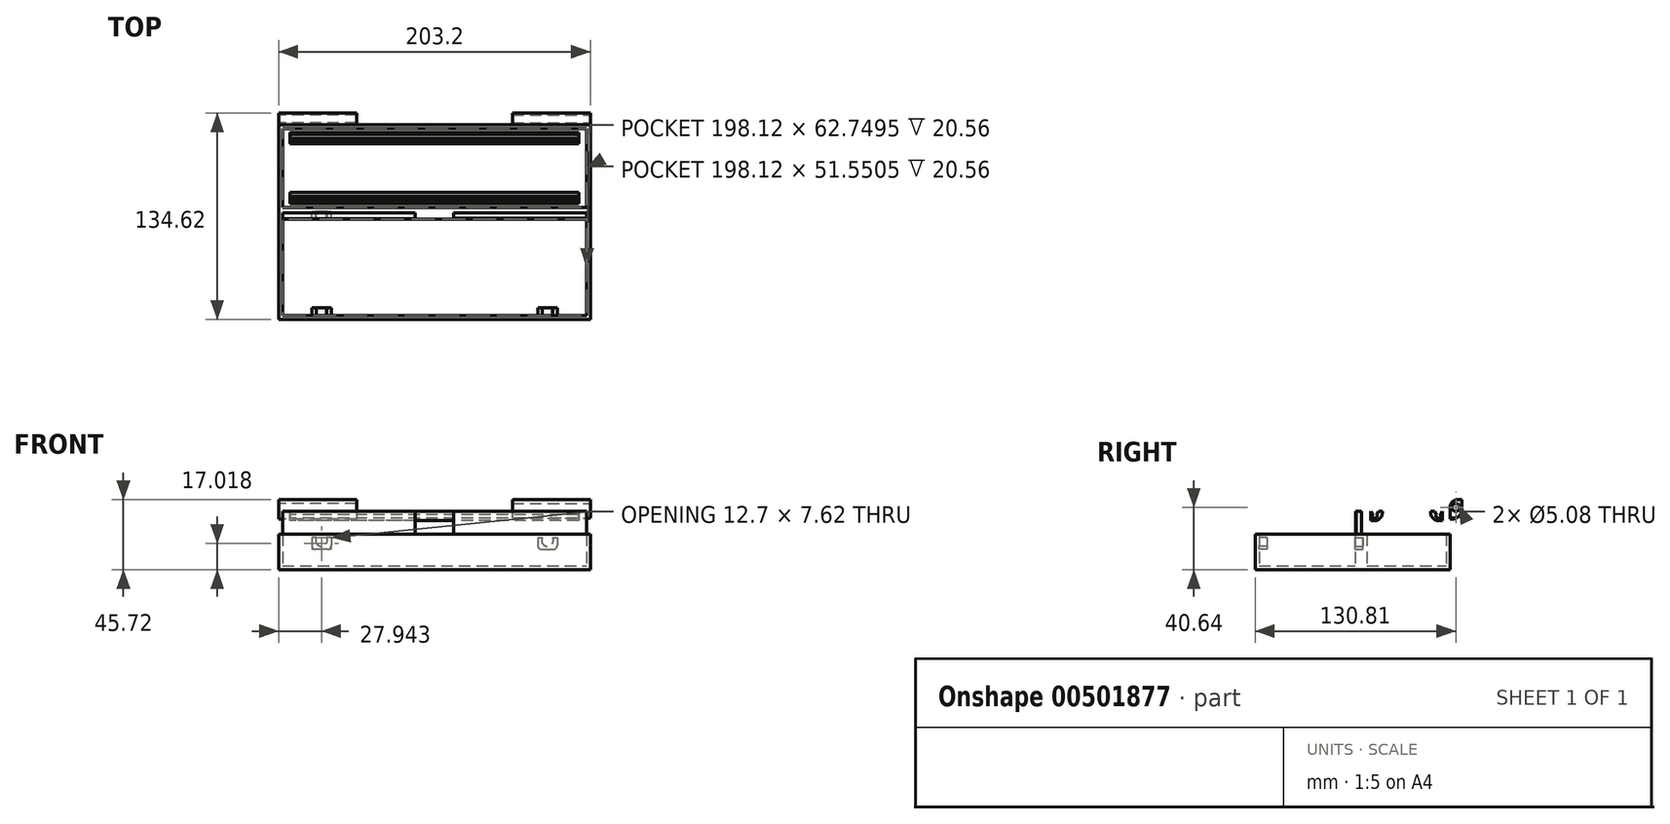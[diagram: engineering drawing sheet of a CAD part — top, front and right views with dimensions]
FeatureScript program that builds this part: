
annotation { "Feature Type Name" : "Feature", "Feature Type Description" : "" }
export const myFeature = defineFeature(function(context is Context, id is Id, definition is map)
    precondition{}
    {
        {
            var Q0;
            Q0=qCreatedBy(makeId("Top.planeOp"),FACE);
            var sketch = newSketch(context, id + "F0", { "sketchPlane" : qUnion([Q0])});
            skLineSegment(sketch, "E0.bottom", {"start": v(-95.04, -72.9) * mm, "end": v(108.16, -72.9) * mm});
            skLineSegment(sketch, "E0.top", {"start": v(-95.04, 54.1) * mm, "end": v(108.16, 54.1) * mm});
            skLineSegment(sketch, "E0.left", {"start": v(-95.04, -72.9) * mm, "end": v(-95.04, 54.1) * mm});
            skLineSegment(sketch, "E0.right", {"start": v(108.16, -72.9) * mm, "end": v(108.16, 54.1) * mm});
            skSolve(sketch);
        }
        {
            var Q0;
            Q0 = qSketchRegion(id + "F0", true);
            extrude(context, id + "F1", {"entities" : qUnion([Q0]), "endBound" : BoundingType.SYMMETRIC, "depth" : 38.1 * mm});
        }
        {
            var Q0;
            Q0=makeQuery(id+"F1.opExtrude","CAP_FACE",FACE,{"disambiguationData":[OSD([sQuery(id+"F0.wireOp",EDGE,"E0.bottom"),sQuery(id+"F0.wireOp",EDGE,"E0.top"),sQuery(id+"F0.wireOp",EDGE,"E0.left"),sQuery(id+"F0.wireOp",EDGE,"E0.right")])],"isStart":false});
            shell(context, id + "F2", {"entities" : qUnion([Q0]), "thickness" : 2.54 * mm});
        }
        {
            var Q0;
            Q0=makeQuery(id+"F2.opShell","OFFSET_FACE",FACE,{"disambiguationData":[OSD([sQuery(id+"F0.wireOp",EDGE,"E0.bottom"),sQuery(id+"F0.wireOp",EDGE,"E0.top"),sQuery(id+"F0.wireOp",EDGE,"E0.left"),sQuery(id+"F0.wireOp",EDGE,"E0.right")])]});
            var sketch = newSketch(context, id + "F3", { "sketchPlane" : qUnion([Q0])});
            skLineSegment(sketch, "E1", {"start": v(-92.5, 0) * mm, "end": v(105.62, 0) * mm});
            skLineSegment(sketch, "E2", {"start": v(-92.5, -2.54) * mm, "end": v(105.62, -2.54) * mm});
            skLineSegment(sketch, "E3", {"start": v(-92.5, 0) * mm, "end": v(-92.5, -2.54) * mm});
            skLineSegment(sketch, "E4", {"start": v(105.62, 0) * mm, "end": v(105.62, -2.54) * mm});
            skSolve(sketch);
        }
        {
            var Q0;
            Q0 = qSketchRegion(id + "F3", true);
            var Q1;
            Q1=makeQuery(id+"F1.opExtrude","CAP_FACE",FACE,{"disambiguationData":[OSD([sQuery(id+"F0.wireOp",EDGE,"E0.bottom"),sQuery(id+"F0.wireOp",EDGE,"E0.top"),sQuery(id+"F0.wireOp",EDGE,"E0.left"),sQuery(id+"F0.wireOp",EDGE,"E0.right")])],"isStart":false});
            extrude(context, id + "F4", {"entities" : qUnion([Q0]), "operationType" : NewBodyOperationType.ADD, "endBound" : BoundingType.UP_TO_SURFACE, "endBoundEntityFace" : qUnion([Q1]), "depth" : 25.4 * mm});
        }
        {
            var Q0;
            Q0=makeQuery(id+"F4.opExtrude","SWEPT_FACE",FACE,{"disambiguationData":[OSD([sQuery(id+"F3.wireOp",EDGE,"E2")])]});
            var sketch = newSketch(context, id + "F5", { "sketchPlane" : qUnion([Q0])});
            skArc(sketch, "E5", {"start": v(76.85, 1.78) * mm, "mid": v(80.22, -3.8) * mm, "end": v(83.6, 1.78) * mm});
            skLineSegment(sketch, "E6", {"start": v(76.85, 1.78) * mm, "end": v(73.87, 1.78) * mm});
            skLineSegment(sketch, "E7", {"start": v(73.87, 1.78) * mm, "end": v(73.87, -3.3) * mm});
            skLineSegment(sketch, "E8", {"start": v(76.41, -5.84) * mm, "end": v(84.03, -5.84) * mm});
            skLineSegment(sketch, "E9", {"start": v(86.57, -3.3) * mm, "end": v(86.57, 1.78) * mm});
            skLineSegment(sketch, "E10", {"start": v(86.57, 1.78) * mm, "end": v(83.6, 1.78) * mm});
            skPoint(sketch, "E11.visualSharp", {"position": v(73.87, -5.84) * mm});
            skArc(sketch, "E11.filletArc", {"start": v(73.87, -3.3) * mm, "mid": v(74.62, -5.1) * mm, "end": v(76.41, -5.84) * mm});
            skPoint(sketch, "E12.visualSharp", {"position": v(86.57, -5.84) * mm});
            skArc(sketch, "E12.filletArc", {"start": v(84.03, -5.84) * mm, "mid": v(85.83, -5.1) * mm, "end": v(86.57, -3.3) * mm});
            skLineSegment(sketch, "E13", {"start": v(6.56, 19.05) * mm, "end": v(6.56, -16.5) * mm, "construction": true});
            skArc(sketch, "E14.MirrorCS", {"start": v(-60.75, -3.3) * mm, "mid": v(-61.5, -5.1) * mm, "end": v(-63.29, -5.84) * mm});
            skPoint(sketch, "E15.MirrorP", {"position": v(-60.75, -5.84) * mm});
            skLineSegment(sketch, "E16.MirrorCS", {"start": v(-63.29, -5.84) * mm, "end": v(-70.9, -5.84) * mm});
            skPoint(sketch, "E17.MirrorP", {"position": v(-73.45, -5.84) * mm});
            skArc(sketch, "E18.MirrorCS", {"start": v(-70.9, -5.84) * mm, "mid": v(-72.7, -5.1) * mm, "end": v(-73.45, -3.3) * mm});
            skLineSegment(sketch, "E19.MirrorCS", {"start": v(-73.45, 1.78) * mm, "end": v(-70.47, 1.78) * mm});
            skLineSegment(sketch, "E20.MirrorCS", {"start": v(-73.45, -3.3) * mm, "end": v(-73.45, 1.78) * mm});
            skArc(sketch, "E21.MirrorCS", {"start": v(-63.73, 1.78) * mm, "mid": v(-67.1, -3.8) * mm, "end": v(-70.47, 1.78) * mm});
            skLineSegment(sketch, "E22.MirrorCS", {"start": v(-63.73, 1.78) * mm, "end": v(-60.75, 1.78) * mm});
            skLineSegment(sketch, "E23.MirrorCS", {"start": v(-60.75, 1.78) * mm, "end": v(-60.75, -3.3) * mm});
            skSolve(sketch);
        }
        {
            var Q0;
            Q0=makeQuery(id+"F5.imprint","IMPRINT",FACE,{"disambiguationData":[TD([[makeQuery(id+"F5.imprint","IMPRINT",EDGE,{"derivedFrom":sQuery(id+"F5.wireOp",EDGE,"E14.MirrorCS")}),-1.0]])]});
            var Q1;
            Q1=makeQuery(id+"F5.imprint","IMPRINT",FACE,{"disambiguationData":[TD([[makeQuery(id+"F5.imprint","IMPRINT",EDGE,{"derivedFrom":sQuery(id+"F5.wireOp",EDGE,"E5")}),-1.0]])]});
            extrude(context, id + "F6", {"entities" : qUnion([Q0, Q1]), "operationType" : NewBodyOperationType.ADD, "depth" : 5.08 * mm});
        }
        {
            var Q0;
            Q0=makeQuery(id+"F2.opShell","OFFSET_FACE",FACE,{"disambiguationData":[OSD([sQuery(id+"F0.wireOp",EDGE,"E0.bottom")])]});
            var sketch = newSketch(context, id + "F7", { "sketchPlane" : qUnion([Q0])});
            skArc(sketch, "E24", {"start": v(-83.6, 1.78) * mm, "mid": v(-80.22, -3.81) * mm, "end": v(-76.85, 1.78) * mm});
            skPoint(sketch, "E25.bottom.start.orphan", {"position": v(-147.3, 0) * mm});
            skLineSegment(sketch, "E26.bottom", {"start": v(-73.87, 1.78) * mm, "end": v(-76.85, 1.78) * mm});
            skLineSegment(sketch, "E26.top", {"start": v(-76.41, -5.84) * mm, "end": v(-84.03, -5.84) * mm});
            skLineSegment(sketch, "E26.left", {"start": v(-73.87, 1.78) * mm, "end": v(-73.87, -3.3) * mm});
            skLineSegment(sketch, "E26.right", {"start": v(-86.57, 1.78) * mm, "end": v(-86.57, -3.3) * mm});
            skPoint(sketch, "E27.visualSharp", {"position": v(-86.57, -5.84) * mm});
            skArc(sketch, "E27.filletArc", {"start": v(-86.57, -3.3) * mm, "mid": v(-85.83, -5.1) * mm, "end": v(-84.03, -5.84) * mm});
            skPoint(sketch, "E28.visualSharp", {"position": v(-73.87, -5.84) * mm});
            skArc(sketch, "E28.filletArc", {"start": v(-76.41, -5.84) * mm, "mid": v(-74.62, -5.1) * mm, "end": v(-73.87, -3.3) * mm});
            skLineSegment(sketch, "E29", {"start": v(-6.56, 19.05) * mm, "end": v(-6.56, -16.51) * mm});
            skLineSegment(sketch, "E30.MirrorCS", {"start": v(63.29, -5.84) * mm, "end": v(70.9, -5.84) * mm});
            skPoint(sketch, "E31.MirrorP", {"position": v(73.45, -5.84) * mm});
            skPoint(sketch, "E32.MirrorP", {"position": v(60.75, -5.84) * mm});
            skArc(sketch, "E33.MirrorCS", {"start": v(63.29, -5.84) * mm, "mid": v(61.5, -5.1) * mm, "end": v(60.75, -3.3) * mm});
            skArc(sketch, "E34.MirrorCS", {"start": v(73.45, -3.3) * mm, "mid": v(72.7, -5.1) * mm, "end": v(70.9, -5.84) * mm});
            skArc(sketch, "E35.MirrorCS", {"start": v(70.47, 1.78) * mm, "mid": v(67.1, -3.81) * mm, "end": v(63.73, 1.78) * mm});
            skLineSegment(sketch, "E36.MirrorCS", {"start": v(60.75, 1.78) * mm, "end": v(63.73, 1.78) * mm});
            skLineSegment(sketch, "E37.MirrorCS", {"start": v(73.45, 1.78) * mm, "end": v(73.45, -3.3) * mm});
            skLineSegment(sketch, "E38.MirrorCS", {"start": v(60.75, 1.78) * mm, "end": v(60.75, -3.3) * mm});
            skLineSegment(sketch, "E39.trimOffspring", {"start": v(-83.6, 1.78) * mm, "end": v(-86.57, 1.78) * mm});
            skLineSegment(sketch, "E40.trimOffspring", {"start": v(70.47, 1.78) * mm, "end": v(73.45, 1.78) * mm});
            skSolve(sketch);
        }
        {
            var Q0;
            Q0 = qSketchRegion(id + "F7", true);
            extrude(context, id + "F8", {"entities" : qUnion([Q0]), "operationType" : NewBodyOperationType.ADD, "depth" : 5.08 * mm});
        }
        {
            var Q0;
            Q0=makeQuery(id+"F1.opExtrude","SWEPT_FACE",FACE,{"disambiguationData":[OSD([sQuery(id+"F0.wireOp",EDGE,"E0.right")])]});
            var sketch = newSketch(context, id + "F9", { "sketchPlane" : qUnion([Q0])});
            skLineSegment(sketch, "E41.bottom", {"start": v(54.1, 14.72) * mm, "end": v(56.63, 14.72) * mm});
            skLineSegment(sketch, "E41.top", {"start": v(59.17, 26.67) * mm, "end": v(61.71, 26.67) * mm});
            skLineSegment(sketch, "E41.left", {"start": v(54.1, 14.72) * mm, "end": v(54.1, 21.59) * mm});
            skLineSegment(sketch, "E41.right", {"start": v(61.71, 19.8) * mm, "end": v(61.71, 26.67) * mm});
            skCircle(sketch, "E42", {"center": v(57.9, 21.59) * mm, "radius": 2.54 * mm});
            skPoint(sketch, "E43.visualSharp", {"position": v(61.71, 14.72) * mm});
            skArc(sketch, "E43.filletArc", {"start": v(56.63, 14.72) * mm, "mid": v(60.22, 16.2) * mm, "end": v(61.71, 19.8) * mm});
            skPoint(sketch, "E44.visualSharp", {"position": v(54.1, 26.67) * mm});
            skArc(sketch, "E44.filletArc", {"start": v(59.17, 26.67) * mm, "mid": v(55.58, 25.18) * mm, "end": v(54.1, 21.59) * mm});
            skSolve(sketch);
        }
        {
            var Q0;
            Q0 = qSketchRegion(id + "F9", true);
            extrude(context, id + "F10", {"entities" : qUnion([Q0]), "operationType" : NewBodyOperationType.ADD, "oppositeDirection" : true, "depth" : 50.8 * mm});
        }
        {
            var Q0;
            Q0=makeQuery(id+"F1.opExtrude","SWEPT_FACE",FACE,{"disambiguationData":[OSD([sQuery(id+"F0.wireOp",EDGE,"E0.left")])]});
            var sketch = newSketch(context, id + "F11", { "sketchPlane" : qUnion([Q0])});
            skLineSegment(sketch, "E45.bottom", {"start": v(-54.1, 13.97) * mm, "end": v(-55.36, 13.97) * mm});
            skLineSegment(sketch, "E45.top", {"start": v(-59.17, 26.67) * mm, "end": v(-61.71, 26.67) * mm});
            skLineSegment(sketch, "E45.left", {"start": v(-54.1, 13.97) * mm, "end": v(-54.1, 21.59) * mm});
            skLineSegment(sketch, "E45.right", {"start": v(-61.71, 20.32) * mm, "end": v(-61.71, 26.67) * mm});
            skCircle(sketch, "E46", {"center": v(-57.9, 21.59) * mm, "radius": 2.54 * mm});
            skPoint(sketch, "E47.visualSharp", {"position": v(-54.1, 26.67) * mm});
            skArc(sketch, "E47.filletArc", {"start": v(-54.1, 21.59) * mm, "mid": v(-55.58, 25.18) * mm, "end": v(-59.17, 26.67) * mm});
            skPoint(sketch, "E48.visualSharp", {"position": v(-61.71, 13.97) * mm});
            skArc(sketch, "E48.filletArc", {"start": v(-61.71, 20.32) * mm, "mid": v(-59.85, 15.83) * mm, "end": v(-55.36, 13.97) * mm});
            skSolve(sketch);
        }
        {
            var Q0;
            {var subQ3=sQuery(id+"F11.wireOp",EDGE,"E45.bottom");Q0=makeQuery(id+"F11.imprint","IMPRINT",FACE,{"disambiguationData":[TD([[makeQuery(id+"F11.imprint","IMPRINT",EDGE,{"derivedFrom":subQ3}),-1.0]])]});}
            extrude(context, id + "F12", {"entities" : qUnion([Q0]), "operationType" : NewBodyOperationType.ADD, "oppositeDirection" : true, "depth" : 50.8 * mm});
        }
        {
            var Q0;
            {var subQ1=sQuery(id+"F0.wireOp",EDGE,"E0.left");var subQ2=sQuery(id+"F0.wireOp",EDGE,"E0.top");Q0=makeQuery(id+"F4.boolean.opBoolean","SPLIT",FACE,{"disambiguationData":[TD([makeQuery(id+"F2.opShell","OFFSET_FACE",FACE,{"disambiguationData":[OSD([subQ2])]})])],"derivedFrom":makeQuery(id+"F2.opShell","OFFSET_FACE",FACE,{"disambiguationData":[OSD([subQ1])]})});}
            var sketch = newSketch(context, id + "F13", { "sketchPlane" : qUnion([Q0])});
            skLineSegment(sketch, "E49.bottom", {"start": v(51.55, 13.05) * mm, "end": v(46.55, 13.05) * mm});
            skLineSegment(sketch, "E49.top", {"start": v(51.55, 19.05) * mm, "end": v(49.05, 19.05) * mm});
            skLineSegment(sketch, "E49.left", {"start": v(51.55, 13.05) * mm, "end": v(51.55, 19.05) * mm});
            skLineSegment(sketch, "E49.right", {"start": v(41.55, 18.05) * mm, "end": v(41.55, 19.05) * mm});
            skArc(sketch, "E50", {"start": v(45.32, 16.9) * mm, "mid": v(46.52, 14.55) * mm, "end": v(47.82, 16.85) * mm});
            skPoint(sketch, "E50.centerSnap0", {"position": v(46.55, 19.05) * mm});
            skPoint(sketch, "E51.visualSharp", {"position": v(41.55, 13.05) * mm});
            skArc(sketch, "E51.filletArc", {"start": v(41.55, 18.05) * mm, "mid": v(43.01, 14.51) * mm, "end": v(46.55, 13.05) * mm});
            skLineSegment(sketch, "E52", {"start": v(47.82, 16.85) * mm, "end": v(49.05, 19.05) * mm});
            skLineSegment(sketch, "E53", {"start": v(45.32, 16.9) * mm, "end": v(44.05, 19.05) * mm});
            skLineSegment(sketch, "E54.trimOffspring", {"start": v(44.05, 19.05) * mm, "end": v(41.55, 19.05) * mm});
            skLineSegment(sketch, "E55", {"start": v(25.78, 19.05) * mm, "end": v(25.78, 4.9) * mm});
            skLineSegment(sketch, "E56.MirrorCS", {"start": v(10, 18.05) * mm, "end": v(10, 19.05) * mm});
            skPoint(sketch, "E57.MirrorP", {"position": v(10, 13.05) * mm});
            skPoint(sketch, "E58.MirrorP", {"position": v(5, 19.05) * mm});
            skLineSegment(sketch, "E59.MirrorCS", {"start": v(0, 13.05) * mm, "end": v(5, 13.05) * mm});
            skLineSegment(sketch, "E60.MirrorCS", {"start": v(0, 19.05) * mm, "end": v(2.5, 19.05) * mm});
            skLineSegment(sketch, "E61.MirrorCS", {"start": v(0, 13.05) * mm, "end": v(0, 19.05) * mm});
            skArc(sketch, "E62.MirrorCS", {"start": v(6.23, 16.9) * mm, "mid": v(5.03, 14.55) * mm, "end": v(3.73, 16.85) * mm});
            skArc(sketch, "E63.MirrorCS", {"start": v(10, 18.05) * mm, "mid": v(8.54, 14.51) * mm, "end": v(5, 13.05) * mm});
            skLineSegment(sketch, "E64.MirrorCS", {"start": v(3.73, 16.85) * mm, "end": v(2.5, 19.05) * mm});
            skLineSegment(sketch, "E65.MirrorCS", {"start": v(6.23, 16.9) * mm, "end": v(7.5, 19.05) * mm});
            skLineSegment(sketch, "E66.MirrorCS", {"start": v(7.5, 19.05) * mm, "end": v(10, 19.05) * mm});
            skSolve(sketch);
        }
        {
            var Q0;
            Q0=makeQuery(id+"F13.imprint","IMPRINT",FACE,{"disambiguationData":[TD([[makeQuery(id+"F13.imprint","IMPRINT",EDGE,{"derivedFrom":sQuery(id+"F13.wireOp",EDGE,"E49.bottom")}),-1.0]])]});
            var Q1;
            Q1=makeQuery(id+"F13.imprint","IMPRINT",FACE,{"disambiguationData":[TD([[makeQuery(id+"F13.imprint","IMPRINT",EDGE,{"derivedFrom":sQuery(id+"F13.wireOp",EDGE,"E56.MirrorCS")}),1.0]])]});
            extrude(context, id + "F14", {"entities" : qUnion([Q0, Q1]), "operationType" : NewBodyOperationType.ADD, "endBound" : BoundingType.UP_TO_NEXT, "depth" : 25 * mm});
        }
        {
            var Q0;
            {var subQ0=sQuery(id+"F0.wireOp",EDGE,"E0.right");var subQ1=sQuery(id+"F0.wireOp",EDGE,"E0.left");var subQ2=sQuery(id+"F0.wireOp",EDGE,"E0.top");var subQ3=sQuery(id+"F0.wireOp",EDGE,"E0.bottom");Q0=makeQuery(id+"F14.boolean.opBoolean","MERGE",FACE,{"derivedFrom":[makeQuery(id+"F4.boolean.opBoolean","MERGE",FACE,{"derivedFrom":[makeQuery(id+"F1.opExtrude","CAP_FACE",FACE,{"disambiguationData":[OSD([subQ3,subQ2,subQ1,subQ0])],"isStart":false}),makeQuery(id+"F4.opExtrude","CAP_FACE",FACE,{"disambiguationData":[OSD([subQ3,subQ2,subQ1,subQ0])],"isStart":false})]}),makeQuery(id+"F14.opExtrude","SWEPT_FACE",FACE,{"disambiguationData":[OSD([sQuery(id+"F13.wireOp",EDGE,"E49.top")])]}),makeQuery(id+"F14.opExtrude","SWEPT_FACE",FACE,{"disambiguationData":[OSD([sQuery(id+"F13.wireOp",EDGE,"E54.trimOffspring")])]})]});}
            var sketch = newSketch(context, id + "F15", { "sketchPlane" : qUnion([Q0])});
            skLineSegment(sketch, "E67.bottom", {"start": v(-87.5, 0.5) * mm, "end": v(-92.5, 0.5) * mm});
            skLineSegment(sketch, "E67.top", {"start": v(-87.5, 51.55) * mm, "end": v(-92.5, 51.55) * mm});
            skLineSegment(sketch, "E67.left", {"start": v(-87.5, 0.5) * mm, "end": v(-87.5, 51.55) * mm});
            skLineSegment(sketch, "E67.right", {"start": v(-92.5, 0.5) * mm, "end": v(-92.5, 51.55) * mm});
            skSolve(sketch);
        }
        {
            var Q0;
            Q0 = qSketchRegion(id + "F15", true);
            extrude(context, id + "F16", {"entities" : qUnion([Q0]), "operationType" : NewBodyOperationType.REMOVE, "oppositeDirection" : true, "depth" : 10 * mm});
        }
        {
            var Q0;
            {var subQ0=sQuery(id+"F15.wireOp",EDGE,"E67.top");Q0=makeQuery(id+"F15.imprint","IMPRINT",FACE,{"disambiguationData":[TD([[makeQuery(id+"F15.imprint","IMPRINT",EDGE,{"derivedFrom":subQ0}),1.0]])]});}
            var Q1;
            {var subQ0=sQuery(id+"F15.wireOp",EDGE,"E67.left");var subQ1=sQuery(id+"F0.wireOp",EDGE,"E0.left");var subQ2=makeQuery(id+"F14.opExtrude","SWEPT_EDGE",EDGE,{"disambiguationData":[OSD([subQ1,sQuery(id+"F13.wireOp",EDGE,"E53"),sQuery(id+"F13.wireOp",EDGE,"E54.trimOffspring")])]});var subQ3=makeQuery(id+"F15.imprint","INTERSECT",VERTEX,{"derivedFrom":[subQ2,subQ0]});Q1=makeQuery(id+"F15.imprint","IMPRINT",FACE,{"disambiguationData":[TD([[makeQuery(id+"F15.imprint","IMPRINT",EDGE,{"disambiguationData":[TD([[subQ3,-1.0]])],"derivedFrom":subQ0}),1.0]])]});}
            var Q2;
            {var subQ0=sQuery(id+"F15.wireOp",EDGE,"E67.left");var subQ1=sQuery(id+"F13.wireOp",EDGE,"E54.trimOffspring");var subQ2=sQuery(id+"F0.wireOp",EDGE,"E0.left");var subQ3=makeQuery(id+"F14.opExtrude","SWEPT_EDGE",EDGE,{"disambiguationData":[OSD([subQ2,sQuery(id+"F13.wireOp",EDGE,"E49.right"),subQ1])]});var subQ4=makeQuery(id+"F15.imprint","INTERSECT",VERTEX,{"derivedFrom":[subQ3,subQ0]});Q2=makeQuery(id+"F15.imprint","IMPRINT",FACE,{"disambiguationData":[TD([[makeQuery(id+"F15.imprint","IMPRINT",EDGE,{"disambiguationData":[TD([[subQ4,-1.0]])],"derivedFrom":subQ0}),1.0]])]});}
            extrude(context, id + "F17", {"entities" : qUnion([Q0, Q1, Q2]), "operationType" : NewBodyOperationType.REMOVE, "oppositeDirection" : true, "depth" : 25 * mm});
        }
        {
            var Q0;
            {var subQ0=sQuery(id+"F0.wireOp",EDGE,"E0.right");var subQ1=sQuery(id+"F0.wireOp",EDGE,"E0.left");var subQ2=sQuery(id+"F0.wireOp",EDGE,"E0.top");var subQ3=sQuery(id+"F0.wireOp",EDGE,"E0.bottom");Q0=makeQuery(id+"F14.boolean.opBoolean","MERGE",FACE,{"derivedFrom":[makeQuery(id+"F4.boolean.opBoolean","MERGE",FACE,{"derivedFrom":[makeQuery(id+"F1.opExtrude","CAP_FACE",FACE,{"disambiguationData":[OSD([subQ3,subQ2,subQ1,subQ0])],"isStart":false}),makeQuery(id+"F4.opExtrude","CAP_FACE",FACE,{"disambiguationData":[OSD([subQ3,subQ2,subQ1,subQ0])],"isStart":false})]}),makeQuery(id+"F14.opExtrude","SWEPT_FACE",FACE,{"disambiguationData":[OSD([sQuery(id+"F13.wireOp",EDGE,"E49.top")])]}),makeQuery(id+"F14.opExtrude","SWEPT_FACE",FACE,{"disambiguationData":[OSD([sQuery(id+"F13.wireOp",EDGE,"E54.trimOffspring")])]})]});}
            var sketch = newSketch(context, id + "F18", { "sketchPlane" : qUnion([Q0])});
            skLineSegment(sketch, "E68.bottom", {"start": v(105.62, 51.55) * mm, "end": v(100.62, 51.55) * mm});
            skLineSegment(sketch, "E68.top", {"start": v(105.62, 0) * mm, "end": v(100.62, 0) * mm});
            skLineSegment(sketch, "E68.left", {"start": v(105.62, 51.55) * mm, "end": v(105.62, 0) * mm});
            skLineSegment(sketch, "E68.right", {"start": v(100.62, 51.55) * mm, "end": v(100.62, 0) * mm});
            skSolve(sketch);
        }
        {
            var Q0;
            {var subQ0=sQuery(id+"F18.wireOp",EDGE,"E68.bottom");Q0=makeQuery(id+"F18.imprint","IMPRINT",FACE,{"disambiguationData":[TD([[makeQuery(id+"F18.imprint","IMPRINT",EDGE,{"derivedFrom":subQ0}),1.0]])]});}
            var Q1;
            {var subQ0=sQuery(id+"F18.wireOp",EDGE,"E68.left");var subQ1=sQuery(id+"F0.wireOp",EDGE,"E0.left");var subQ2=makeQuery(id+"F14.opExtrude","SWEPT_EDGE",EDGE,{"disambiguationData":[OSD([subQ1,sQuery(id+"F13.wireOp",EDGE,"E49.top"),sQuery(id+"F13.wireOp",EDGE,"E52")])]});var subQ3=makeQuery(id+"F18.imprint","INTERSECT",VERTEX,{"derivedFrom":[subQ2,subQ0]});var subQ4=makeQuery(id+"F14.opExtrude","SWEPT_EDGE",EDGE,{"disambiguationData":[OSD([subQ1,sQuery(id+"F13.wireOp",EDGE,"E53"),sQuery(id+"F13.wireOp",EDGE,"E54.trimOffspring")])]});var subQ5=makeQuery(id+"F18.imprint","INTERSECT",VERTEX,{"derivedFrom":[subQ4,subQ0]});Q1=makeQuery(id+"F18.imprint","IMPRINT",FACE,{"disambiguationData":[TD([[makeQuery(id+"F18.imprint","IMPRINT",EDGE,{"disambiguationData":[TD([[subQ3,1.0],[subQ5,-1.0]])],"derivedFrom":subQ0}),1.0]])]});}
            var Q2;
            {var subQ0=sQuery(id+"F18.wireOp",EDGE,"E68.left");var subQ1=sQuery(id+"F13.wireOp",EDGE,"E54.trimOffspring");var subQ2=sQuery(id+"F0.wireOp",EDGE,"E0.left");var subQ3=makeQuery(id+"F14.opExtrude","SWEPT_EDGE",EDGE,{"disambiguationData":[OSD([subQ2,sQuery(id+"F13.wireOp",EDGE,"E49.right"),subQ1])]});var subQ4=makeQuery(id+"F18.imprint","INTERSECT",VERTEX,{"derivedFrom":[subQ3,subQ0]});var subQ5=makeQuery(id+"F14.opExtrude","SWEPT_EDGE",EDGE,{"disambiguationData":[OSD([subQ2,sQuery(id+"F13.wireOp",EDGE,"E53"),subQ1])]});var subQ6=makeQuery(id+"F18.imprint","INTERSECT",VERTEX,{"derivedFrom":[subQ5,subQ0]});Q2=makeQuery(id+"F18.imprint","IMPRINT",FACE,{"disambiguationData":[TD([[makeQuery(id+"F18.imprint","IMPRINT",EDGE,{"disambiguationData":[TD([[subQ4,1.0],[subQ6,-1.0]])],"derivedFrom":subQ0}),-1.0]])]});}
            var Q3;
            {var subQ0=sQuery(id+"F18.wireOp",EDGE,"E68.left");var subQ1=sQuery(id+"F13.wireOp",EDGE,"E66.MirrorCS");var subQ2=sQuery(id+"F0.wireOp",EDGE,"E0.left");var subQ3=makeQuery(id+"F14.opExtrude","SWEPT_EDGE",EDGE,{"disambiguationData":[OSD([subQ2,sQuery(id+"F13.wireOp",EDGE,"E56.MirrorCS"),subQ1])]});var subQ4=makeQuery(id+"F18.imprint","INTERSECT",VERTEX,{"derivedFrom":[subQ3,subQ0]});var subQ5=makeQuery(id+"F14.opExtrude","SWEPT_EDGE",EDGE,{"disambiguationData":[OSD([subQ2,sQuery(id+"F13.wireOp",EDGE,"E65.MirrorCS"),subQ1])]});var subQ6=makeQuery(id+"F18.imprint","INTERSECT",VERTEX,{"derivedFrom":[subQ5,subQ0]});Q3=makeQuery(id+"F18.imprint","IMPRINT",FACE,{"disambiguationData":[TD([[makeQuery(id+"F18.imprint","IMPRINT",EDGE,{"disambiguationData":[TD([[subQ4,-1.0],[subQ6,1.0]])],"derivedFrom":subQ0}),-1.0]])]});}
            var Q4;
            {var subQ0=sQuery(id+"F18.wireOp",EDGE,"E68.left");var subQ1=sQuery(id+"F0.wireOp",EDGE,"E0.left");var subQ2=makeQuery(id+"F14.opExtrude","SWEPT_EDGE",EDGE,{"disambiguationData":[OSD([subQ1,sQuery(id+"F13.wireOp",EDGE,"E60.MirrorCS"),sQuery(id+"F13.wireOp",EDGE,"E64.MirrorCS")])]});var subQ3=makeQuery(id+"F18.imprint","INTERSECT",VERTEX,{"derivedFrom":[subQ2,subQ0]});var subQ4=makeQuery(id+"F14.opExtrude","SWEPT_EDGE",EDGE,{"disambiguationData":[OSD([subQ1,sQuery(id+"F13.wireOp",EDGE,"E65.MirrorCS"),sQuery(id+"F13.wireOp",EDGE,"E66.MirrorCS")])]});var subQ5=makeQuery(id+"F18.imprint","INTERSECT",VERTEX,{"derivedFrom":[subQ4,subQ0]});Q4=makeQuery(id+"F18.imprint","IMPRINT",FACE,{"disambiguationData":[TD([[makeQuery(id+"F18.imprint","IMPRINT",EDGE,{"disambiguationData":[TD([[subQ3,-1.0],[subQ5,1.0]])],"derivedFrom":subQ0}),1.0]])]});}
            var Q5;
            {var subQ0=sQuery(id+"F18.wireOp",EDGE,"E68.top");Q5=makeQuery(id+"F18.imprint","IMPRINT",FACE,{"disambiguationData":[TD([[makeQuery(id+"F18.imprint","IMPRINT",EDGE,{"derivedFrom":subQ0}),-1.0]])]});}
            extrude(context, id + "F19", {"entities" : qUnion([Q0, Q1, Q2, Q3, Q4, Q5]), "operationType" : NewBodyOperationType.REMOVE, "oppositeDirection" : true, "depth" : 15 * mm});
        }
        {
            var Q0;
            {var subQ1=sQuery(id+"F0.wireOp",EDGE,"E0.left");var subQ3=sQuery(id+"F0.wireOp",EDGE,"E0.bottom");Q0=makeQuery(id+"F4.boolean.opBoolean","SPLIT",FACE,{"disambiguationData":[TD([makeQuery(id+"F2.opShell","OFFSET_FACE",FACE,{"disambiguationData":[OSD([subQ3])]})])],"derivedFrom":makeQuery(id+"F2.opShell","OFFSET_FACE",FACE,{"disambiguationData":[OSD([subQ1])]})});}
            var sketch = newSketch(context, id + "F20", { "sketchPlane" : qUnion([Q0])});
            skLineSegment(sketch, "E69.top", {"start": v(-2.54, 7.05) * mm, "end": v(-5.54, 7.05) * mm});
            skLineSegment(sketch, "E69.left", {"start": v(-2.54, 19.05) * mm, "end": v(-2.54, 7.05) * mm});
            skLineSegment(sketch, "E69.right", {"start": v(-5.54, 9.05) * mm, "end": v(-5.54, 7.05) * mm});
            skLineSegment(sketch, "E70", {"start": v(-3.54, 19.05) * mm, "end": v(-3.54, 9.05) * mm});
            skPoint(sketch, "E71.start.orphan", {"position": v(-5.54, 9.05) * mm});
            skLineSegment(sketch, "E72", {"start": v(-3.54, 9.05) * mm, "end": v(-5.54, 9.05) * mm});
            skLineSegment(sketch, "E73", {"start": v(-3.54, 19.05) * mm, "end": v(-2.54, 19.05) * mm});
            skSolve(sketch);
        }
        {
            var Q0;
            Q0=makeQuery(id+"F20.imprint","IMPRINT",FACE,{"disambiguationData":[TD([[makeQuery(id+"F20.imprint","IMPRINT",EDGE,{"derivedFrom":sQuery(id+"F20.wireOp",EDGE,"E69.top")}),-1.0]])]});
            extrude(context, id + "F21", {"entities" : qUnion([Q0]), "operationType" : NewBodyOperationType.ADD, "endBound" : BoundingType.UP_TO_NEXT, "depth" : 25 * mm});
        }
        {
            var Q0;
            {var subQ0=sQuery(id+"F0.wireOp",EDGE,"E0.right");var subQ8=sQuery(id+"F0.wireOp",EDGE,"E0.bottom");var subQ16=sQuery(id+"F0.wireOp",EDGE,"E0.left");var subQ17=sQuery(id+"F0.wireOp",EDGE,"E0.top");Q0=makeQuery(id+"F21.boolean.opBoolean","MERGE",FACE,{"derivedFrom":[makeQuery(id+"F19.boolean.opBoolean","SPLIT",FACE,{"disambiguationData":[TD([makeQuery(id+"F1.opExtrude","SWEPT_FACE",FACE,{"disambiguationData":[OSD([subQ8])]})])],"derivedFrom":makeQuery(id+"F14.boolean.opBoolean","MERGE",FACE,{"derivedFrom":[makeQuery(id+"F4.boolean.opBoolean","MERGE",FACE,{"derivedFrom":[makeQuery(id+"F1.opExtrude","CAP_FACE",FACE,{"disambiguationData":[OSD([subQ8,subQ17,subQ16,subQ0])],"isStart":false}),makeQuery(id+"F4.opExtrude","CAP_FACE",FACE,{"disambiguationData":[OSD([subQ8,subQ17,subQ16,subQ0])],"isStart":false})]}),makeQuery(id+"F14.opExtrude","SWEPT_FACE",FACE,{"disambiguationData":[OSD([sQuery(id+"F13.wireOp",EDGE,"E49.top")])]}),makeQuery(id+"F14.opExtrude","SWEPT_FACE",FACE,{"disambiguationData":[OSD([sQuery(id+"F13.wireOp",EDGE,"E54.trimOffspring")])]})]})}),makeQuery(id+"F21.opExtrude","SWEPT_FACE",FACE,{"disambiguationData":[OSD([sQuery(id+"F20.wireOp",EDGE,"E73")])]})]});}
            var sketch = newSketch(context, id + "F22", { "sketchPlane" : qUnion([Q0])});
            skLineSegment(sketch, "E74.bottom", {"start": v(-92.5, -3.54) * mm, "end": v(-6, -3.54) * mm});
            skLineSegment(sketch, "E74.top", {"start": v(-92.5, -7.32) * mm, "end": v(-6, -7.32) * mm});
            skLineSegment(sketch, "E74.left", {"start": v(-92.5, -3.54) * mm, "end": v(-92.5, -7.32) * mm});
            skLineSegment(sketch, "E74.right", {"start": v(-6, -3.54) * mm, "end": v(-6, -7.32) * mm});
            skLineSegment(sketch, "E75.bottom", {"start": v(19.12, -3.54) * mm, "end": v(105.62, -3.54) * mm});
            skLineSegment(sketch, "E75.top", {"start": v(19.12, -7.03) * mm, "end": v(105.62, -7.03) * mm});
            skLineSegment(sketch, "E75.left", {"start": v(19.12, -3.54) * mm, "end": v(19.12, -7.03) * mm});
            skLineSegment(sketch, "E75.right", {"start": v(105.62, -3.54) * mm, "end": v(105.62, -7.03) * mm});
            skSolve(sketch);
        }
        {
            var Q0;
            Q0=makeQuery(id+"F22.imprint","IMPRINT",FACE,{"disambiguationData":[TD([[makeQuery(id+"F22.imprint","IMPRINT",EDGE,{"derivedFrom":sQuery(id+"F22.wireOp",EDGE,"E74.bottom")}),1.0]])]});
            var Q1;
            Q1=makeQuery(id+"F22.imprint","IMPRINT",FACE,{"disambiguationData":[TD([[makeQuery(id+"F22.imprint","IMPRINT",EDGE,{"derivedFrom":sQuery(id+"F22.wireOp",EDGE,"E75.bottom")}),1.0]])]});
            extrude(context, id + "F23", {"entities" : qUnion([Q0, Q1]), "operationType" : NewBodyOperationType.REMOVE, "oppositeDirection" : true, "depth" : 15 * mm});
        }
    });
